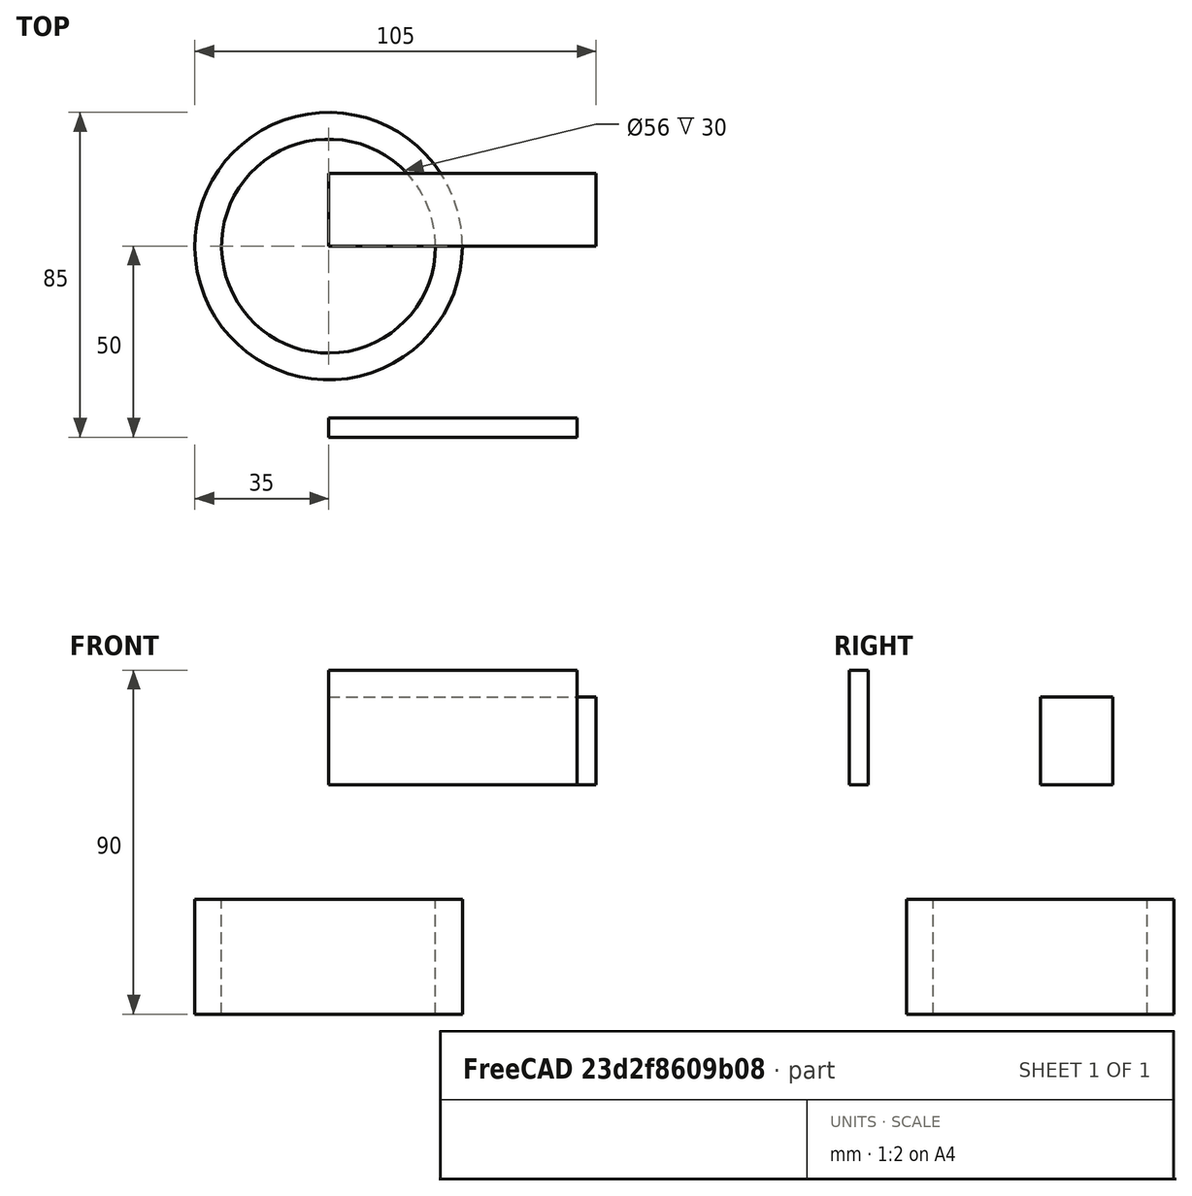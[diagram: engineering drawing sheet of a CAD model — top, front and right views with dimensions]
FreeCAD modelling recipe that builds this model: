
FCSTD DOCUMENT  (FreeCAD 0.18R16131 (Git))
Label: chassy
License: All rights reserved
LicenseURL: http://en.wikipedia.org/wiki/All_rights_reserved
objects: Part::Box×2, Part::Cylinder×2, Sketcher::SketchObject×1, PartDesign::Body×1, Part::Cut×1
note: 7 computed .brp shape members not serialized (recipe doc carries the construction recipe); baked Part::Feature solids carry a one-line shape summary decoded from their .brp

FEATURE [Sketcher::SketchObject] Sketch
  MapMode = 5
  Support = -> [XY_Plane]
  sketch-geometry (12):
    g0: LineSegment StartX=0 StartY=0 StartZ=0 EndX=0 EndY=19.859 EndZ=0
    g1: LineSegment StartX=5.79353 StartY=30.5085 StartZ=0 EndX=5.79353 EndY=50.4681 EndZ=0
    g2: LineSegment StartX=0.299714 StartY=59.4795 StartZ=0 EndX=0.299714 EndY=79.8343 EndZ=0
    g3: LineSegment StartX=59.4101 StartY=80.1288 StartZ=0 EndX=59.4101 EndY=59.4919 EndZ=0
    g4: LineSegment StartX=54.6931 StartY=50.6475 StartZ=0 EndX=54.6931 EndY=29.1262 EndZ=0
    g5: LineSegment StartX=60.8842 StartY=-0.944772 StartZ=0 EndX=61.179 EndY=19.987 EndZ=0
    g6: ArcOfCircle CenterX=67.1097 CenterY=49.404 CenterZ=0 NormalX=0 NormalY=0 NormalZ=1 AngleXU=0 Radius=12.6905 StartAngle=2.22272 EndAngle=3.02672
    g7: ArcOfCircle CenterX=67.5049 CenterY=29.2469 CenterZ=0 NormalX=0 NormalY=0 NormalZ=1 AngleXU=0 Radius=11.5231 StartAngle=3.18771 EndAngle=4.17197
    g8: ArcOfCircle CenterX=-5.81181 CenterY=28.0612 CenterZ=0 NormalX=0 NormalY=0 NormalZ=1 AngleXU=0 Radius=10.7516 StartAngle=5.34119 EndAngle=6.49102
    g9: ArcOfCircle CenterX=-5.61419 CenterY=49.9969 CenterZ=0 NormalX=0 NormalY=0 NormalZ=1 AngleXU=0 Radius=11.8637 StartAngle=0.033321 EndAngle=0.977446
    g10: ArcOfCircle CenterX=30.1549 CenterY=35.7683 CenterZ=0 NormalX=0 NormalY=0 NormalZ=1 AngleXU=0 Radius=48.3796 StartAngle=4.01194 EndAngle=5.41393
    g11: ArcOfCircle CenterX=29.7218 CenterY=26.7282 CenterZ=0 NormalX=0 NormalY=0 NormalZ=1 AngleXU=0 Radius=60.7057 StartAngle=1.05817 EndAngle=2.07789
  constraints (5):
    c: Vertical(g0)
    c: Vertical(g2)
    c: Vertical(g1)
    c: Vertical(g3)
    c: Vertical(g4)
FEATURE [PartDesign::Body] Body  label="chassy"
  Group = -> [Sketch]
  Origin = -> Origin
FEATURE [Part::Box] Box  label="motor"
  AttacherType = Attacher::AttachEngine3D
  Height = 23
  Length = 70
  Width = 19
FEATURE [Part::Cylinder] Cylinder  label="external"
  Angle = 360
  AttacherType = Attacher::AttachEngine3D
  Height = 30
  Radius = 35
FEATURE [Part::Cylinder] Cylinder001  label="internal"
  Angle = 360
  AttacherType = Attacher::AttachEngine3D
  Height = 30
  Radius = 28
FEATURE [Part::Cut] Cut  label="wheel"
  Base = -> Cylinder
  Placement = pos=(0,0,-60) rot=(0,0,1;0rad)
  Tool = -> Cylinder001
FEATURE [Part::Box] Box001  label="pizero"
  AttacherType = Attacher::AttachEngine3D
  Height = 30
  Length = 65
  Placement = pos=(0,-50,0) rot=(0,0,1;0rad)
  Width = 5
